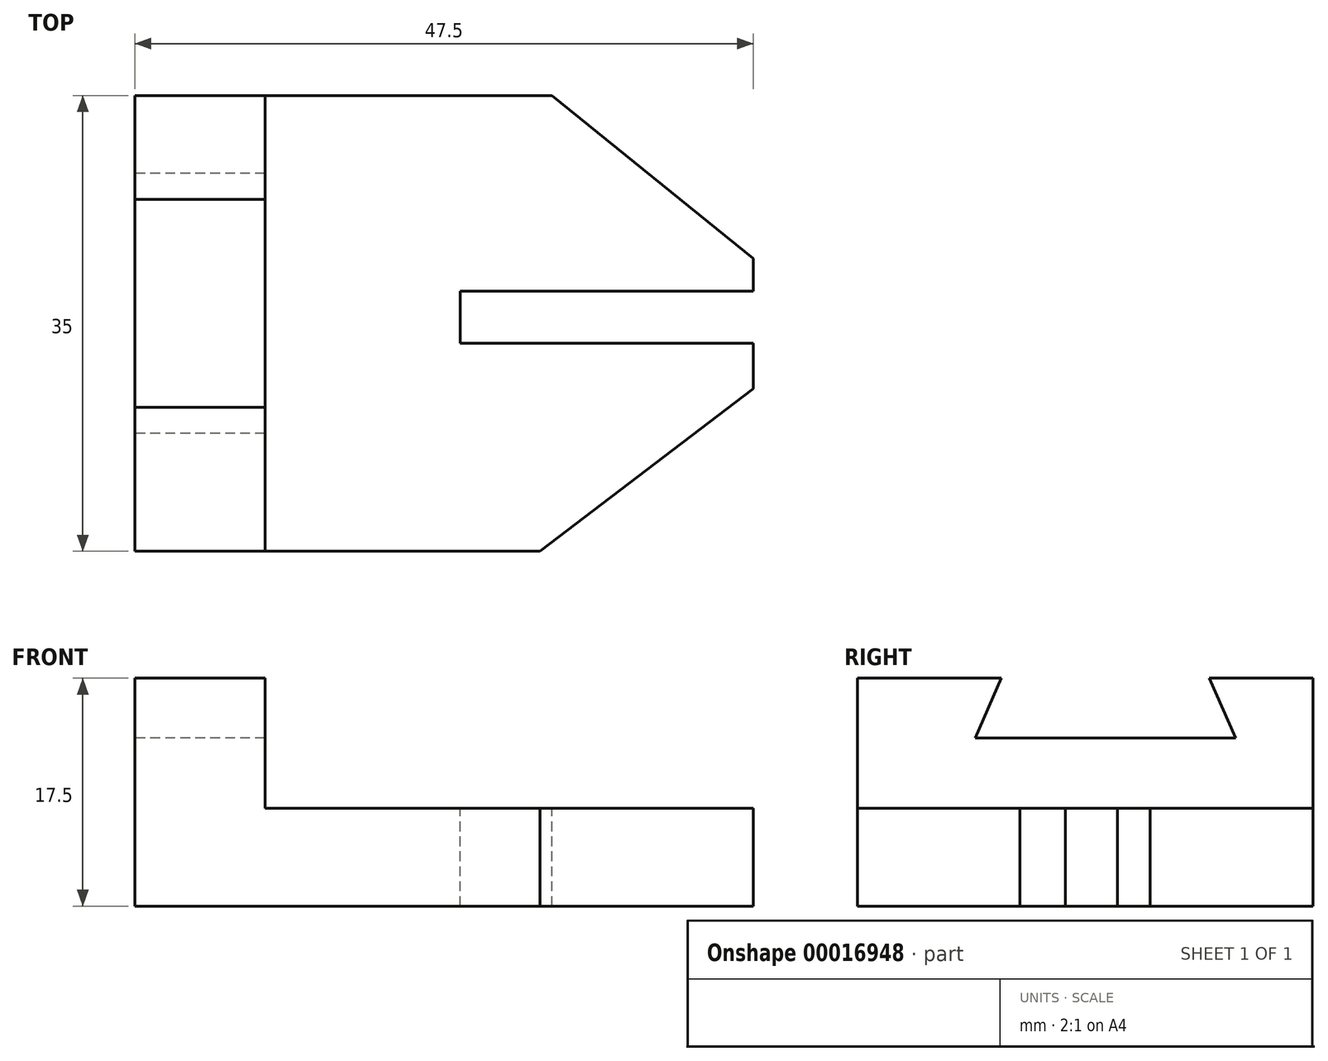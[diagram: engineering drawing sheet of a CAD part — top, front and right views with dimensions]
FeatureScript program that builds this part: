
annotation { "Feature Type Name" : "Feature", "Feature Type Description" : "" }
export const myFeature = defineFeature(function(context is Context, id is Id, definition is map)
    precondition{}
    {
        {
            var Q0;
            Q0=qCreatedBy(makeId("Top.planeOp"),FACE);
            var sketch = newSketch(context, id + "F0", { "sketchPlane" : qUnion([Q0])});
            skLineSegment(sketch, "E0.bottom", {"start": v(-14.8, 32.44) * mm, "end": v(20.2, 32.44) * mm});
            skLineSegment(sketch, "E0.top", {"start": v(-14.8, -15.06) * mm, "end": v(20.2, -15.06) * mm});
            skLineSegment(sketch, "E0.left", {"start": v(-14.8, 32.44) * mm, "end": v(-14.8, -15.06) * mm});
            skLineSegment(sketch, "E0.right", {"start": v(20.2, 32.44) * mm, "end": v(20.2, -15.06) * mm});
            skSolve(sketch);
        }
        {
            var Q0;
            Q0=makeQuery(id+"F0.imprint","IMPRINT",FACE,{"disambiguationData":[TD([[makeQuery(id+"F0.imprint","IMPRINT",EDGE,{"derivedFrom":sQuery(id+"F0.wireOp",EDGE,"E0.bottom")}),-1.0]])]});
            extrude(context, id + "F1", {"entities" : qUnion([Q0]), "depth" : 7.5 * mm});
        }
        {
            var Q0;
            Q0=makeQuery(id+"F1.opExtrude","SWEPT_BODY",BODY,{"disambiguationData":[OSD([sQuery(id+"F0.wireOp",EDGE,"E0.bottom"),sQuery(id+"F0.wireOp",EDGE,"E0.top"),sQuery(id+"F0.wireOp",EDGE,"E0.left"),sQuery(id+"F0.wireOp",EDGE,"E0.right")])]});
            var Q1;
            Q1=makeQuery(id+"F1.opExtrude","SWEPT_EDGE",EDGE,{"disambiguationData":[OSD([sQuery(id+"F0.wireOp",EDGE,"E0.top"),sQuery(id+"F0.wireOp",EDGE,"E0.right")])]});
            transform(context, id + "F2", {"entities" : qUnion([Q0]), "transformType" : TransformType.ROTATION, "transformAxis" : qUnion([Q1]), "angle" : 90 * degree, "makeCopy" : false});
        }
        {
            var Q0;
            Q0=makeQuery(id+"F1.opExtrude","CAP_FACE",FACE,{"disambiguationData":[OSD([sQuery(id+"F0.wireOp",EDGE,"E0.bottom"),sQuery(id+"F0.wireOp",EDGE,"E0.top"),sQuery(id+"F0.wireOp",EDGE,"E0.left"),sQuery(id+"F0.wireOp",EDGE,"E0.right")])],"isStart":false});
            var sketch = newSketch(context, id + "F3", { "sketchPlane" : qUnion([Q0])});
            skLineSegment(sketch, "E1", {"start": v(52.26, 19.94) * mm, "end": v(67.7, 7.44) * mm});
            skLineSegment(sketch, "E2", {"start": v(67.7, 7.44) * mm, "end": v(67.7, 19.94) * mm});
            skLineSegment(sketch, "E3", {"start": v(67.7, 19.94) * mm, "end": v(52.26, 19.94) * mm});
            skLineSegment(sketch, "E4", {"start": v(51.32, -15.06) * mm, "end": v(67.7, -2.56) * mm});
            skLineSegment(sketch, "E5", {"start": v(67.7, -2.56) * mm, "end": v(67.7, -15.06) * mm});
            skLineSegment(sketch, "E6", {"start": v(67.7, -15.06) * mm, "end": v(51.32, -15.06) * mm});
            skLineSegment(sketch, "E7", {"start": v(67.7, 4.92) * mm, "end": v(45.2, 4.92) * mm});
            skLineSegment(sketch, "E8", {"start": v(45.2, 4.92) * mm, "end": v(45.2, 0.92) * mm});
            skLineSegment(sketch, "E9", {"start": v(45.2, 0.92) * mm, "end": v(67.7, 0.92) * mm});
            skLineSegment(sketch, "E10", {"start": v(67.7, 4.92) * mm, "end": v(67.7, 0.92) * mm});
            skSolve(sketch);
        }
        {
            var Q0;
            Q0=makeQuery(id+"F3.imprint","IMPRINT",FACE,{"disambiguationData":[TD([[makeQuery(id+"F3.imprint","IMPRINT",EDGE,{"derivedFrom":sQuery(id+"F3.wireOp",EDGE,"E1")}),1.0]])]});
            var Q1;
            Q1=makeQuery(id+"F3.imprint","IMPRINT",FACE,{"disambiguationData":[TD([[makeQuery(id+"F3.imprint","IMPRINT",EDGE,{"derivedFrom":sQuery(id+"F3.wireOp",EDGE,"E4")}),-1.0]])]});
            var Q2;
            Q2=makeQuery(id+"F3.imprint","IMPRINT",FACE,{"disambiguationData":[TD([[makeQuery(id+"F3.imprint","IMPRINT",EDGE,{"derivedFrom":sQuery(id+"F3.wireOp",EDGE,"E7")}),1.0]])]});
            extrude(context, id + "F4", {"entities" : qUnion([Q0, Q1, Q2]), "operationType" : NewBodyOperationType.REMOVE, "endBound" : BoundingType.THROUGH_ALL, "oppositeDirection" : true, "depth" : 25 * mm});
        }
        {
            var Q0;
            Q0=makeQuery(id+"F1.opExtrude","CAP_FACE",FACE,{"disambiguationData":[OSD([sQuery(id+"F0.wireOp",EDGE,"E0.bottom"),sQuery(id+"F0.wireOp",EDGE,"E0.top"),sQuery(id+"F0.wireOp",EDGE,"E0.left"),sQuery(id+"F0.wireOp",EDGE,"E0.right")])],"isStart":false});
            var sketch = newSketch(context, id + "F5", { "sketchPlane" : qUnion([Q0])});
            skLineSegment(sketch, "E11", {"start": v(30.2, 19.94) * mm, "end": v(30.2, -15.06) * mm});
            skLineSegment(sketch, "E12", {"start": v(30.2, 19.94) * mm, "end": v(20.2, 19.94) * mm});
            skLineSegment(sketch, "E13", {"start": v(20.2, 19.94) * mm, "end": v(20.2, -15.06) * mm});
            skLineSegment(sketch, "E14", {"start": v(20.2, -15.06) * mm, "end": v(30.2, -15.06) * mm});
            skSolve(sketch);
        }
        {
            var Q0;
            Q0=makeQuery(id+"F5.imprint","IMPRINT",FACE,{"disambiguationData":[TD([[makeQuery(id+"F5.imprint","IMPRINT",EDGE,{"derivedFrom":sQuery(id+"F5.wireOp",EDGE,"E11")}),-1.0]])]});
            extrude(context, id + "F6", {"entities" : qUnion([Q0]), "operationType" : NewBodyOperationType.ADD, "depth" : 10 * mm});
        }
        {
            var Q0;
            Q0=makeQuery(id+"F6.boolean.opBoolean","MERGE",FACE,{"derivedFrom":[makeQuery(id+"F1.opExtrude","SWEPT_FACE",FACE,{"disambiguationData":[OSD([sQuery(id+"F0.wireOp",EDGE,"E0.top")])]}),makeQuery(id+"F6.opExtrude","SWEPT_FACE",FACE,{"disambiguationData":[OSD([sQuery(id+"F5.wireOp",EDGE,"E13")])]})]});
            var sketch = newSketch(context, id + "F7", { "sketchPlane" : qUnion([Q0])});
            skLineSegment(sketch, "E15", {"start": v(-11.97, 17.5) * mm, "end": v(-13.98, 12.92) * mm});
            skLineSegment(sketch, "E16", {"start": v(-13.98, 12.92) * mm, "end": v(6.02, 12.92) * mm});
            skLineSegment(sketch, "E17", {"start": v(6.02, 12.92) * mm, "end": v(4, 17.5) * mm});
            skLineSegment(sketch, "E18", {"start": v(4, 17.5) * mm, "end": v(-11.97, 17.5) * mm});
            skSolve(sketch);
        }
        {
            var Q0;
            Q0=makeQuery(id+"F7.imprint","IMPRINT",FACE,{"disambiguationData":[TD([[makeQuery(id+"F7.imprint","IMPRINT",EDGE,{"derivedFrom":sQuery(id+"F7.wireOp",EDGE,"E15")}),1.0]])]});
            extrude(context, id + "F8", {"entities" : qUnion([Q0]), "operationType" : NewBodyOperationType.REMOVE, "endBound" : BoundingType.THROUGH_ALL, "oppositeDirection" : true, "depth" : 25 * mm});
        }
    });
